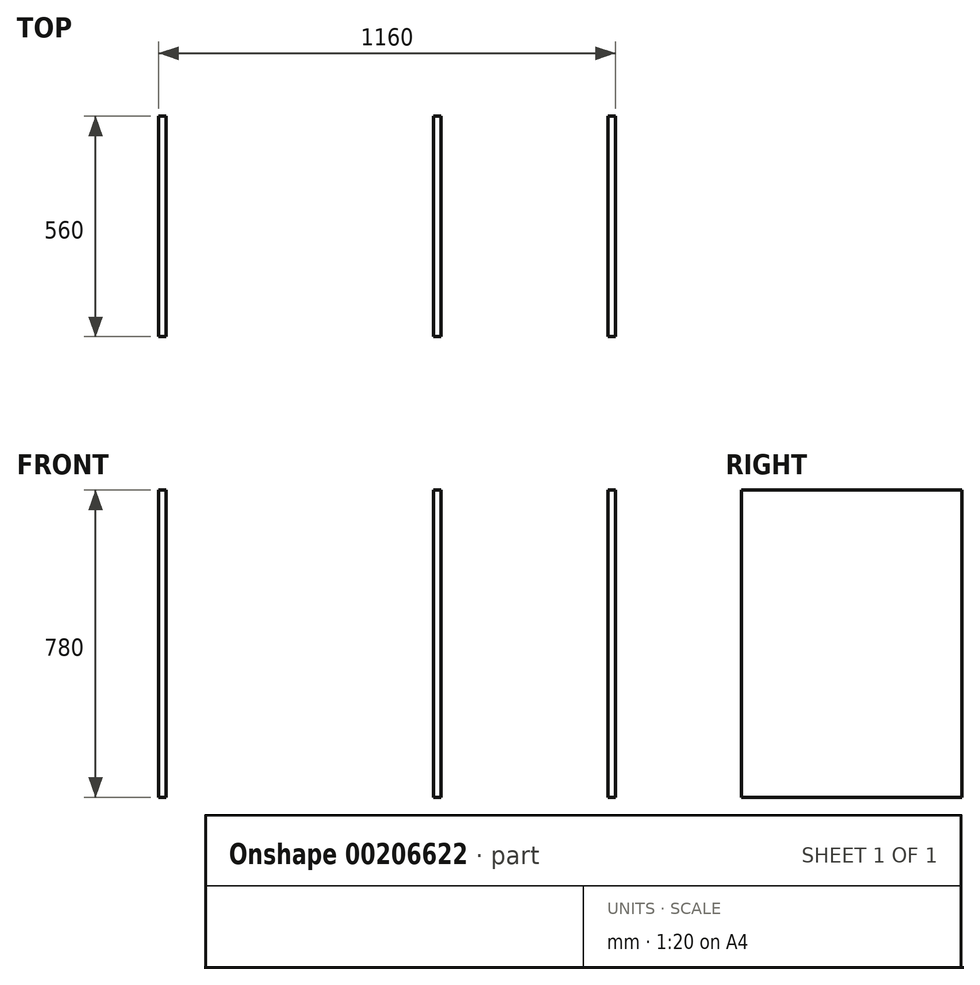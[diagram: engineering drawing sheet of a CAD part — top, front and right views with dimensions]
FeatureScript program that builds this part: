
annotation { "Feature Type Name" : "Feature", "Feature Type Description" : "" }
export const myFeature = defineFeature(function(context is Context, id is Id, definition is map)
    precondition{}
    {
        {
            var Q0;
            Q0=qCreatedBy(makeId("Front.planeOp"),FACE);
            var sketch = newSketch(context, id + "F0", { "sketchPlane" : qUnion([Q0])});
            skLineSegment(sketch, "E0.bottom", {"start": v(-580, -390) * mm, "end": v(580, -390) * mm});
            skLineSegment(sketch, "E0.top", {"start": v(-580, 390) * mm, "end": v(580, 390) * mm});
            skLineSegment(sketch, "E0.left", {"start": v(-580, -390) * mm, "end": v(-580, 390) * mm});
            skLineSegment(sketch, "E0.right", {"start": v(580, -390) * mm, "end": v(580, 390) * mm});
            skPoint(sketch, "E0.middle", {"position": v(0, 0) * mm});
            skLineSegment(sketch, "E1", {"start": v(-561, 390) * mm, "end": v(-561, -390) * mm});
            skLineSegment(sketch, "E2", {"start": v(-401, 390) * mm, "end": v(-401, -390) * mm});
            skLineSegment(sketch, "E3", {"start": v(-382, 390) * mm, "end": v(-382, -390) * mm});
            skLineSegment(sketch, "E4", {"start": v(-561, -330) * mm, "end": v(-401, -330) * mm});
            skLineSegment(sketch, "E5", {"start": v(561, 390) * mm, "end": v(561, -390) * mm});
            skLineSegment(sketch, "E6", {"start": v(118, 390) * mm, "end": v(118, -390) * mm});
            skLineSegment(sketch, "E7", {"start": v(137, 390) * mm, "end": v(137, -390) * mm});
            skLineSegment(sketch, "E8", {"start": v(137, -330) * mm, "end": v(561, -330) * mm});
            skLineSegment(sketch, "E9", {"start": v(-382, 216) * mm, "end": v(118, 216) * mm});
            skLineSegment(sketch, "E10", {"start": v(137, 120) * mm, "end": v(561, 120) * mm});
            skLineSegment(sketch, "E11", {"start": v(137, 139) * mm, "end": v(561, 139) * mm});
            skLineSegment(sketch, "E12", {"start": v(-382, 235) * mm, "end": v(118, 235) * mm});
            skLineSegment(sketch, "E13", {"start": v(-561, 289) * mm, "end": v(-401, 289) * mm});
            skLineSegment(sketch, "E14", {"start": v(-382, 270) * mm, "end": v(-561, 270) * mm});
            skSolve(sketch);
        }
        {
            var Q0;
            {var subQ0=sQuery(id+"F0.wireOp",EDGE,"E0.left");Q0=makeQuery(id+"F0.imprint","IMPRINT",FACE,{"disambiguationData":[TD([[makeQuery(id+"F0.imprint","IMPRINT",EDGE,{"derivedFrom":subQ0}),-1.0]])]});}
            extrude(context, id + "F1", {"entities" : qUnion([Q0]), "depth" : 560 * mm});
        }
        {
            var Q0;
            {var subQ4=sQuery(id+"F0.wireOp",EDGE,"E0.right");Q0=makeQuery(id+"F0.imprint","IMPRINT",FACE,{"disambiguationData":[TD([[makeQuery(id+"F0.imprint","IMPRINT",EDGE,{"derivedFrom":subQ4}),1.0]])]});}
            extrude(context, id + "F2", {"entities" : qUnion([Q0]), "depth" : 560 * mm});
        }
        {
            var Q0;
            {var subQ0=sQuery(id+"F0.wireOp",EDGE,"E6");var subQ7=sQuery(id+"F0.wireOp",EDGE,"E0.bottom");var subQ8=makeQuery(id+"F0.imprint","INTERSECT",VERTEX,{"derivedFrom":[subQ7,subQ0]});Q0=makeQuery(id+"F0.imprint","IMPRINT",FACE,{"disambiguationData":[TD([[makeQuery(id+"F0.imprint","IMPRINT",EDGE,{"disambiguationData":[TD([[subQ8,-1.0]])],"derivedFrom":subQ7}),1.0]])]});}
            extrude(context, id + "F3", {"entities" : qUnion([Q0]), "depth" : 560 * mm});
        }
    });
